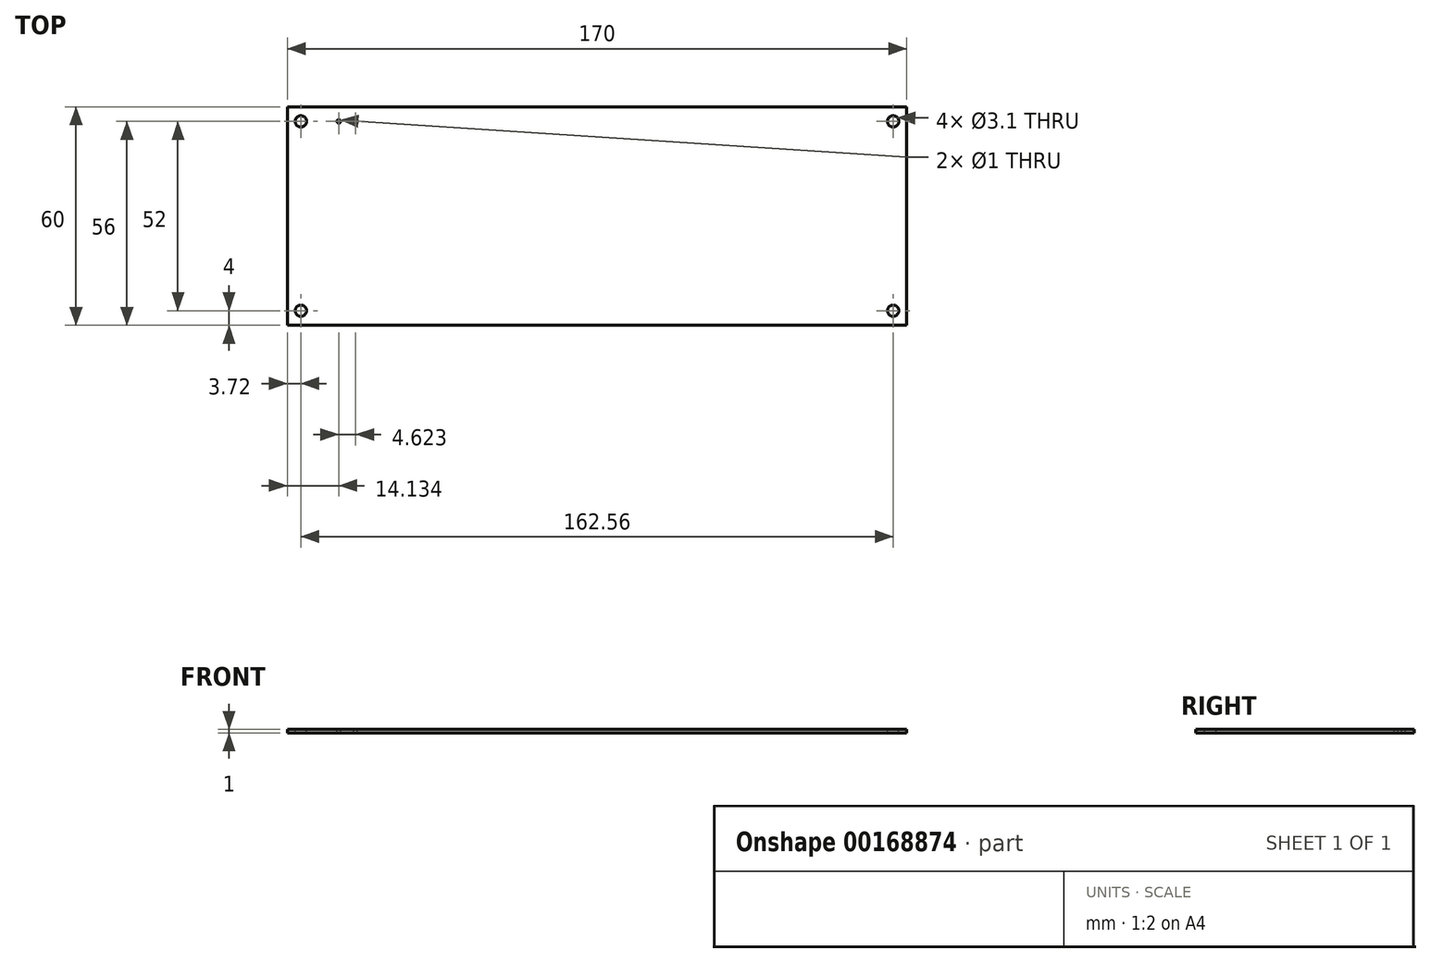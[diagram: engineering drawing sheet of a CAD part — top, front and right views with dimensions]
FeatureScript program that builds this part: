
annotation { "Feature Type Name" : "Feature", "Feature Type Description" : "" }
export const myFeature = defineFeature(function(context is Context, id is Id, definition is map)
    precondition{}
    {
        {
            var Q0;
            Q0=qCreatedBy(makeId("Top.planeOp"),FACE);
            var sketch = newSketch(context, id + "F0", { "sketchPlane" : qUnion([Q0])});
            skLineSegment(sketch, "E0.bottom", {"start": v(85, -30) * mm, "end": v(-85, -30) * mm});
            skLineSegment(sketch, "E0.top", {"start": v(85, 30) * mm, "end": v(-85, 30) * mm});
            skLineSegment(sketch, "E0.left", {"start": v(85, -30) * mm, "end": v(85, 30) * mm});
            skLineSegment(sketch, "E0.right", {"start": v(-85, -30) * mm, "end": v(-85, 30) * mm});
            skLineSegment(sketch, "E1", {"start": v(-170.5, 26) * mm, "end": v(178.25, 26) * mm, "construction": true});
            skLineSegment(sketch, "E2", {"start": v(-81.28, -113.97) * mm, "end": v(-81.28, 30) * mm, "construction": true});
            skLineSegment(sketch, "E3.MirrorCS", {"start": v(-170.5, -26) * mm, "end": v(178.25, -26) * mm, "construction": true});
            skLineSegment(sketch, "E4.MirrorCS", {"start": v(81.28, -113.97) * mm, "end": v(81.28, 30) * mm, "construction": true});
            skPoint(sketch, "E5", {"position": v(-81.28, 26) * mm});
            skPoint(sketch, "E6", {"position": v(81.28, 26) * mm});
            skPoint(sketch, "E7", {"position": v(81.28, -26) * mm});
            skPoint(sketch, "E8", {"position": v(-81.28, -26) * mm});
            skPoint(sketch, "E9", {"position": v(-70.87, 26) * mm});
            skPoint(sketch, "E10", {"position": v(-66.24, 26) * mm});
            skSolve(sketch);
        }
        {
            var Q0;
            Q0=makeQuery(id+"F0.imprint","IMPRINT",FACE,{"disambiguationData":[TD([[makeQuery(id+"F0.imprint","IMPRINT",EDGE,{"derivedFrom":sQuery(id+"F0.wireOp",EDGE,"E0.bottom")}),-1.0]])]});
            extrude(context, id + "F1", {"entities" : qUnion([Q0]), "oppositeDirection" : true, "depth" : 1 * mm});
        }
        {
            var Q0;
            Q0=sQuery(id+"F0.wireOp",VERTEX,"E5");
            var Q1;
            Q1=sQuery(id+"F0.wireOp",VERTEX,"E8");
            var Q2;
            Q2=sQuery(id+"F0.wireOp",VERTEX,"E6");
            var Q3;
            Q3=sQuery(id+"F0.wireOp",VERTEX,"E7");
            var Q4;
            Q4=makeQuery(id+"F1.opExtrude","SWEPT_BODY",BODY,{"disambiguationData":[OSD([sQuery(id+"F0.wireOp",EDGE,"E0.bottom"),sQuery(id+"F0.wireOp",EDGE,"E0.top"),sQuery(id+"F0.wireOp",EDGE,"E0.left"),sQuery(id+"F0.wireOp",EDGE,"E0.right")])]});
            hole(context, id + "F2", {"style" : HoleStyle.SIMPLE, "endStyle" : HoleEndStyle.THROUGH, "holeDiameter" : 3.1 * mm, "startFromSketch" : true, "locations" : qUnion([Q0, Q1, Q2, Q3]), "scope" : qUnion([Q4]), "isTappedThrough" : true});
        }
        {
            var Q0;
            Q0=sQuery(id+"F0.wireOp",VERTEX,"E9");
            var Q1;
            Q1=sQuery(id+"F0.wireOp",VERTEX,"E10");
            var Q2;
            Q2=makeQuery(id+"F1.opExtrude","SWEPT_BODY",BODY,{"disambiguationData":[OSD([sQuery(id+"F0.wireOp",EDGE,"E0.bottom"),sQuery(id+"F0.wireOp",EDGE,"E0.top"),sQuery(id+"F0.wireOp",EDGE,"E0.left"),sQuery(id+"F0.wireOp",EDGE,"E0.right")])]});
            hole(context, id + "F3", {"style" : HoleStyle.SIMPLE, "endStyle" : HoleEndStyle.THROUGH, "holeDiameter" : 1 * mm, "locations" : qUnion([Q0, Q1]), "scope" : qUnion([Q2]), "isTappedThrough" : true});
        }
    });
